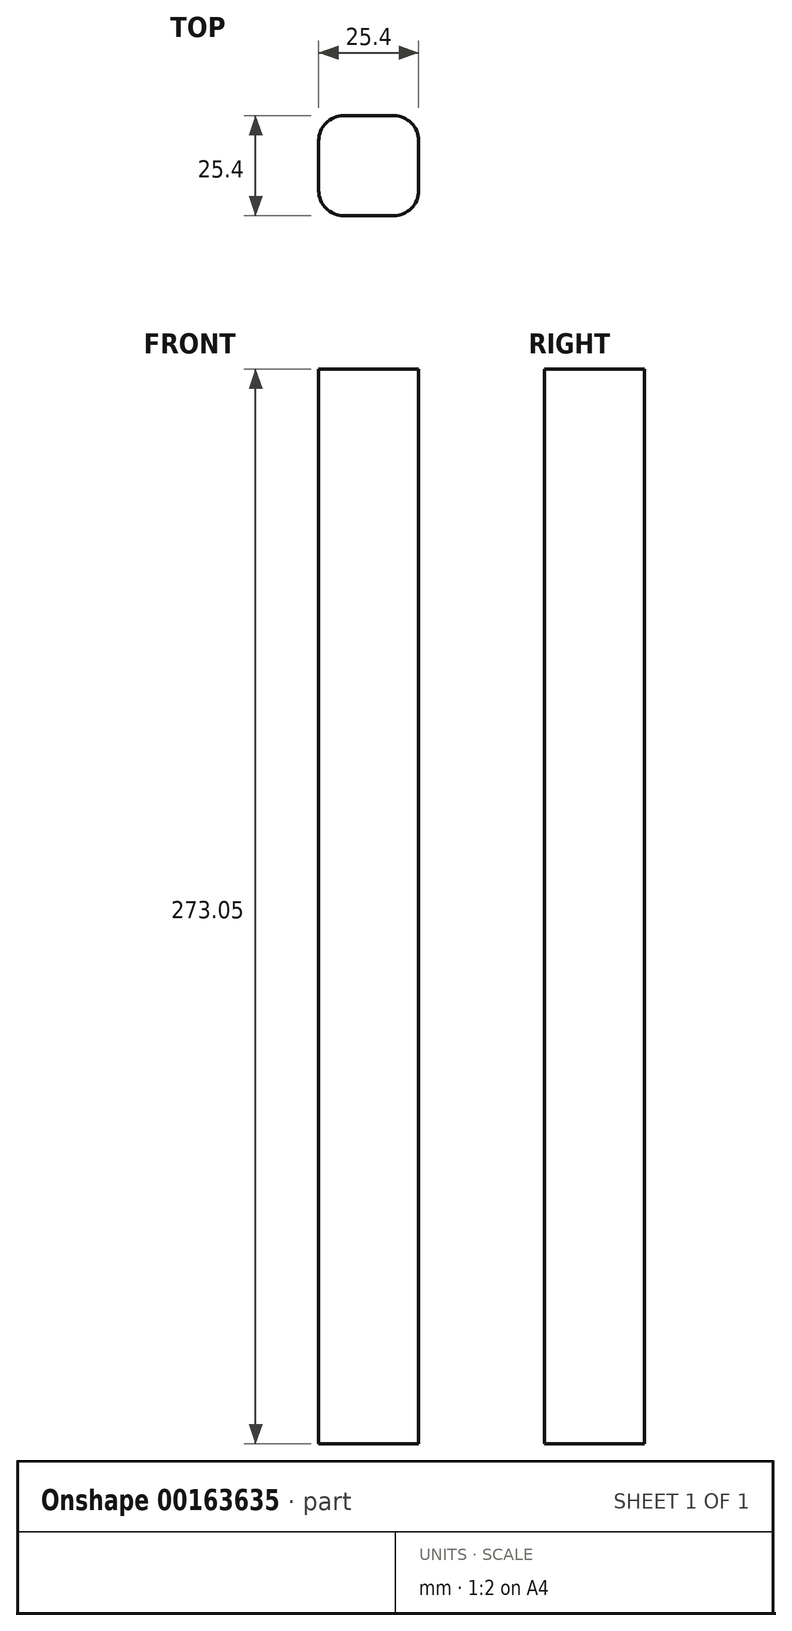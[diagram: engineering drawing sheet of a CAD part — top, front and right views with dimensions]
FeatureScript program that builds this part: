
annotation { "Feature Type Name" : "Feature", "Feature Type Description" : "" }
export const myFeature = defineFeature(function(context is Context, id is Id, definition is map)
    precondition{}
    {
        {
            var Q0;
            Q0=qCreatedBy(makeId("Top.planeOp"),FACE);
            var sketch = newSketch(context, id + "F0", { "sketchPlane" : qUnion([Q0])});
            skLineSegment(sketch, "E0.bottom", {"start": v(6.35, 12.7) * mm, "end": v(-6.35, 12.7) * mm});
            skLineSegment(sketch, "E0.top", {"start": v(6.35, -12.7) * mm, "end": v(-6.35, -12.7) * mm});
            skLineSegment(sketch, "E0.left", {"start": v(12.7, 6.35) * mm, "end": v(12.7, -6.35) * mm});
            skLineSegment(sketch, "E0.right", {"start": v(-12.7, 6.35) * mm, "end": v(-12.7, -6.35) * mm});
            skPoint(sketch, "E0.middle", {"position": v(0, 0) * mm});
            skPoint(sketch, "E1.visualSharp", {"position": v(-12.7, 12.7) * mm});
            skArc(sketch, "E1.filletArc", {"start": v(-6.35, 12.7) * mm, "mid": v(-10.84, 10.84) * mm, "end": v(-12.7, 6.35) * mm});
            skPoint(sketch, "E2.visualSharp", {"position": v(-12.7, -12.7) * mm});
            skArc(sketch, "E2.filletArc", {"start": v(-12.7, -6.35) * mm, "mid": v(-10.84, -10.84) * mm, "end": v(-6.35, -12.7) * mm});
            skPoint(sketch, "E3.visualSharp", {"position": v(12.7, -12.7) * mm});
            skArc(sketch, "E3.filletArc", {"start": v(6.35, -12.7) * mm, "mid": v(10.84, -10.84) * mm, "end": v(12.7, -6.35) * mm});
            skPoint(sketch, "E4.visualSharp", {"position": v(12.7, 12.7) * mm});
            skArc(sketch, "E4.filletArc", {"start": v(12.7, 6.35) * mm, "mid": v(10.84, 10.84) * mm, "end": v(6.35, 12.7) * mm});
            skSolve(sketch);
        }
        {
            var Q0;
            Q0=qSketchRegion(id+"F0",true);
            extrude(context, id + "F1", {"entities" : qUnion([Q0]), "depth" : 273.05 * mm, "offsetDistance" : 25.4 * mm});
        }
    });
